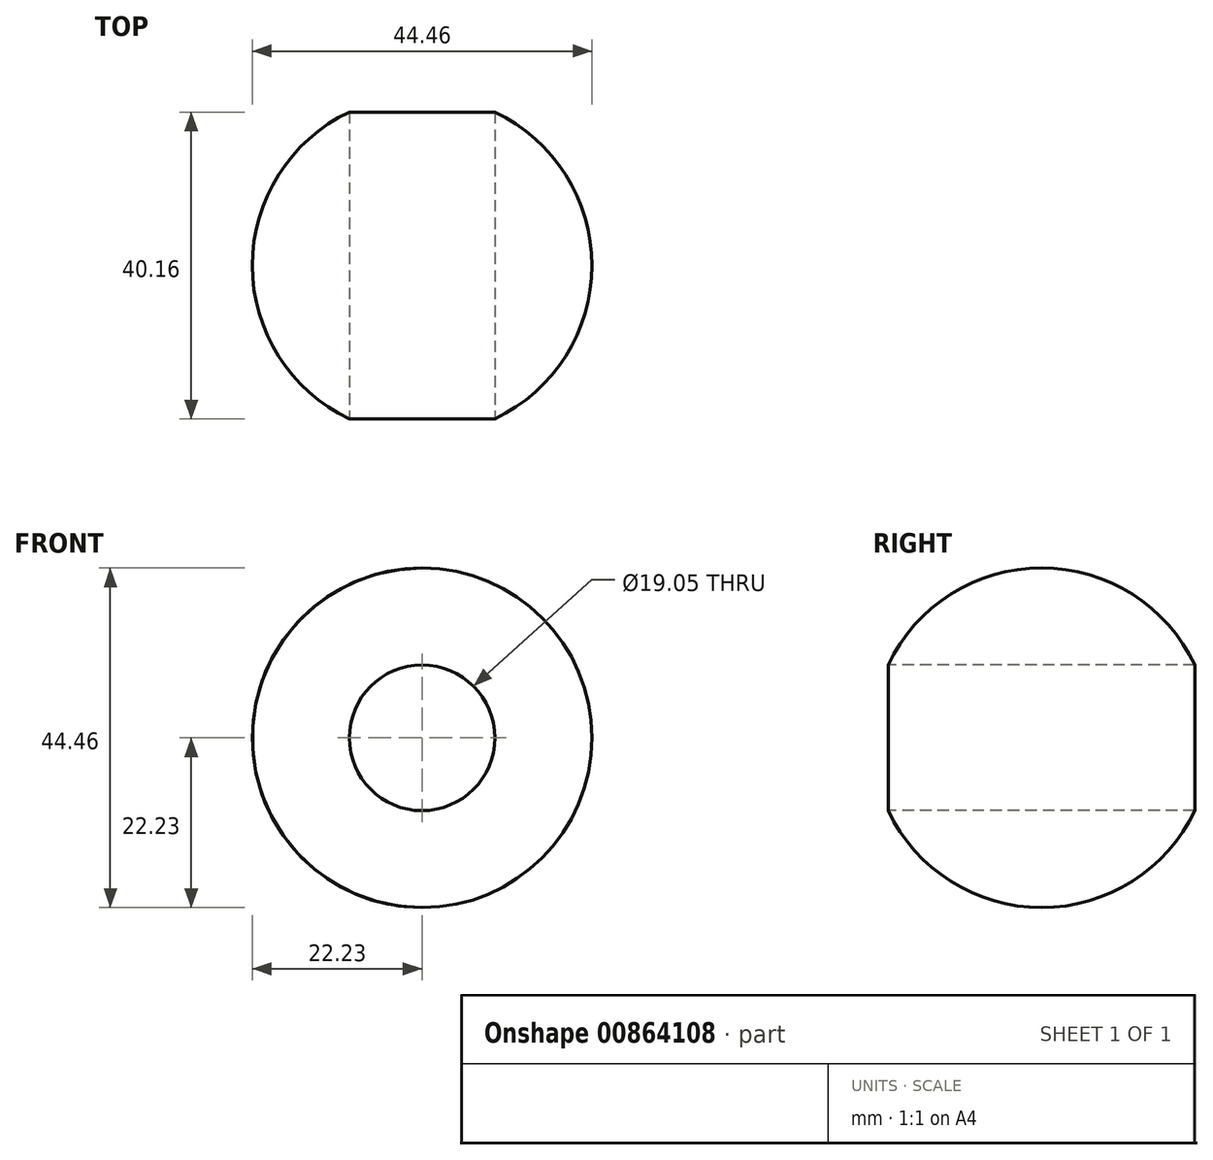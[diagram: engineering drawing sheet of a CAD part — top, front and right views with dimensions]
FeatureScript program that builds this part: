
annotation { "Feature Type Name" : "Feature", "Feature Type Description" : "" }
export const myFeature = defineFeature(function(context is Context, id is Id, definition is map)
    precondition{}
    {
        {
            var Q0;
            Q0=qCreatedBy(makeId("Front.planeOp"),FACE);
            var sketch = newSketch(context, id + "F0", { "sketchPlane" : qUnion([Q0])});
            skArc(sketch, "E0", {"start": v(0, 22.23) * mm, "mid": v(-22.23, 0) * mm, "end": v(0, -22.23) * mm});
            skLineSegment(sketch, "E1", {"start": v(0, 22.23) * mm, "end": v(0, -22.23) * mm});
            skSolve(sketch);
        }
        {
            var Q0;
            Q0=makeQuery(id+"F0.imprint","IMPRINT",FACE,{"disambiguationData":[TD([[makeQuery(id+"F0.imprint","IMPRINT",EDGE,{"derivedFrom":sQuery(id+"F0.wireOp",EDGE,"E0")}),1.0]])]});
            var Q1;
            Q1=sQuery(id+"F0.wireOp",EDGE,"E1");
            revolve(context, id + "F1", {"surfaceOperationType" : NewSurfaceOperationType.NEW, "entities" : qUnion([Q0]), "axis" : qUnion([Q1]), "revolveType" : RevolveType.FULL});
        }
        {
            var Q0;
            Q0=qCreatedBy(makeId("Front.planeOp"),FACE);
            var sketch = newSketch(context, id + "F2", { "sketchPlane" : qUnion([Q0])});
            skCircle(sketch, "E2", {"center": v(0, 0) * mm, "radius": 9.53 * mm});
            skSolve(sketch);
        }
        {
            var Q0;
            Q0 = qSketchRegion(id + "F2", true);
            extrude(context, id + "F3", {"entities" : qUnion([Q0]), "operationType" : NewBodyOperationType.REMOVE, "oppositeDirection" : true, "depth" : 76.2 * mm, "offsetDistance" : 25.4 * mm, "symmetric" : true});
        }
    });
